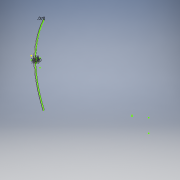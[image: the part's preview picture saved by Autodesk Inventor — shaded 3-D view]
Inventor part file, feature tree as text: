
AUTODESK INVENTOR PART (.ipt)
format: ipt  version: 2018 (Build 220112000, 112)  size: 443,904 bytes
history: native  units: in
note: dims shown in document units (in); Inventor stores cm internally (conversion verified against a paired STEP export)
features: fillet x8, extrude x4, mirror x2, sketch x1
ambient origin geometry x8: Origin, YZ Plane, XZ Plane, XY Plane, X Axis, Y Axis, Z Axis, Center Point
bodies: Body1 (feature_tree)
feature tree (15):
  sketch  "Sketch1"  dims[d4=0.07in d7=0.15in d14=0.15in d15=0.05in d20=0.1in d21=0.0in d22=0.15in d23=0.0in d25=0.05in d26=0.02in d27=0.02in d28=0.01in d29=0.05in d30=0.15in d31=0.0in d32=0.01in d33=0.01in d34=0.15in d35=0.0in d36=0.01in d37=0.01in d38=0.01in]
  extrude  "Extrusion2"  Depth=0.15in
  extrude  "Extrusion3"  Depth=0.15in
  fillet  "Fillet1"  Radius=0.05in
  fillet  "Fillet2"  Radius=0.1in
  fillet  "Fillet3"  Radius=0.15in
  extrude  "Extrusion4"  Depth=0.01in
  fillet  "Fillet4"  Radius=0.02in
  mirror  "Mirror1"
  mirror  "Mirror2"
  fillet  "Fillet5"  Radius=0.02in
  extrude  "Extrusion5"  Depth=0.01in
  fillet  "Fillet6"  Radius=0.05in
  fillet  "Fillet7"  Radius=0.15in
  fillet  "Fillet8"  Radius=0.01in
